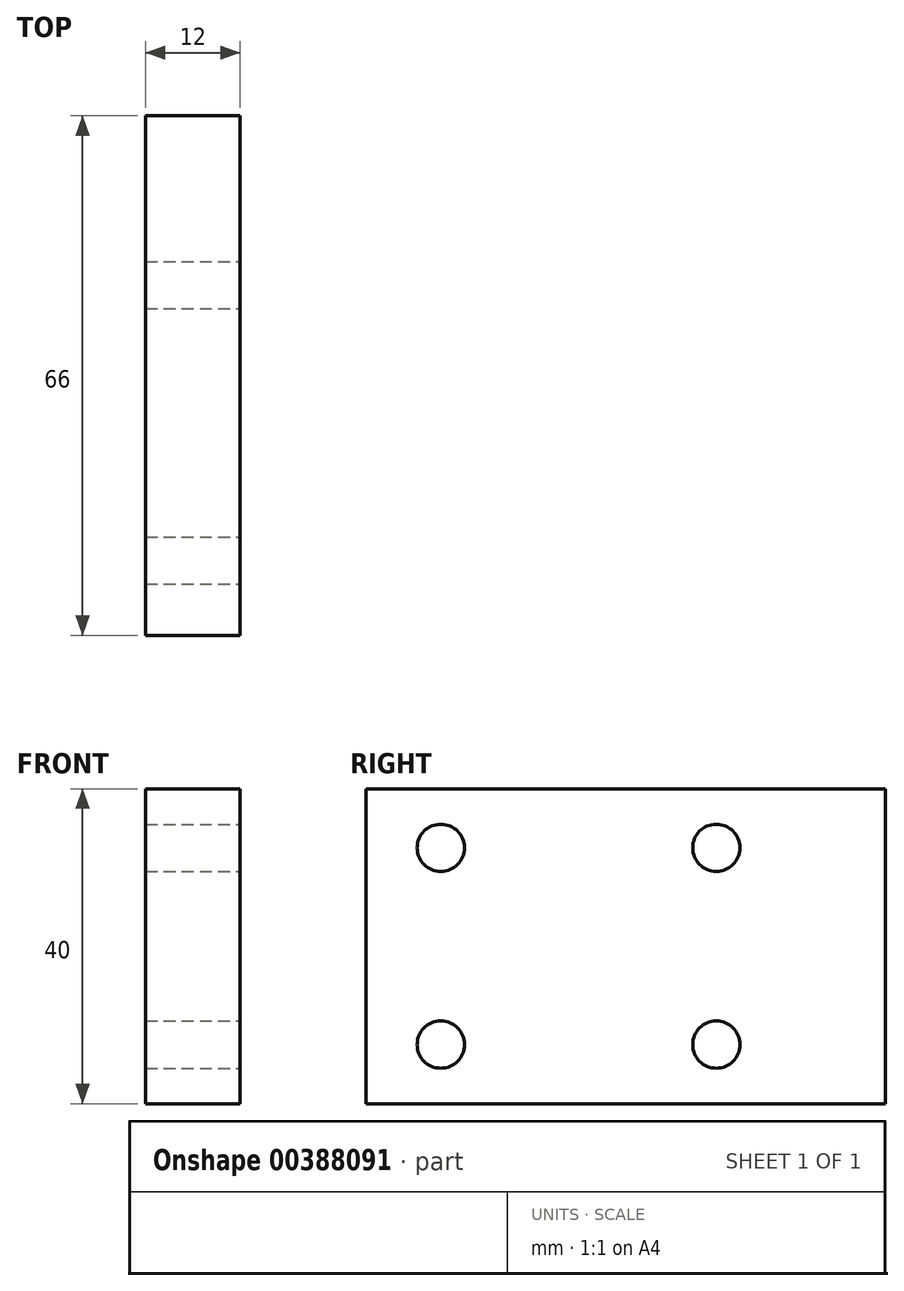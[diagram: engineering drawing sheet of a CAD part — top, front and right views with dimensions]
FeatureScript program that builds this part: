
annotation { "Feature Type Name" : "Feature", "Feature Type Description" : "" }
export const myFeature = defineFeature(function(context is Context, id is Id, definition is map)
    precondition{}
    {
        {
            var Q0;
            Q0=qCreatedBy(makeId("Right.planeOp"),FACE);
            var sketch = newSketch(context, id + "F0", { "sketchPlane" : qUnion([Q0])});
            skLineSegment(sketch, "E0.bottom", {"start": v(0, 0) * mm, "end": v(66, 0) * mm});
            skLineSegment(sketch, "E0.top", {"start": v(0, 40) * mm, "end": v(66, 40) * mm});
            skLineSegment(sketch, "E0.left", {"start": v(0, 0) * mm, "end": v(0, 40) * mm});
            skLineSegment(sketch, "E0.right", {"start": v(66, 0) * mm, "end": v(66, 40) * mm});
            skSolve(sketch);
        }
        {
            var Q0;
            Q0=makeQuery(id+"F0.imprint","IMPRINT",FACE,{"disambiguationData":[TD([[makeQuery(id+"F0.imprint","IMPRINT",EDGE,{"derivedFrom":sQuery(id+"F0.wireOp",EDGE,"E0.bottom")}),1.0]])]});
            extrude(context, id + "F1", {"entities" : qUnion([Q0]), "depth" : 12 * mm});
        }
        {
            var Q0;
            Q0=makeQuery(id+"F1.opExtrude","CAP_FACE",FACE,{"disambiguationData":[OSD([sQuery(id+"F0.wireOp",EDGE,"E0.bottom"),sQuery(id+"F0.wireOp",EDGE,"E0.top"),sQuery(id+"F0.wireOp",EDGE,"E0.left"),sQuery(id+"F0.wireOp",EDGE,"E0.right")])],"isStart":false});
            var sketch = newSketch(context, id + "F2", { "sketchPlane" : qUnion([Q0])});
            skLineSegment(sketch, "E1", {"start": v(0, 0) * mm, "end": v(9.5, 0) * mm, "construction": true});
            skLineSegment(sketch, "E2", {"start": v(9.5, 0) * mm, "end": v(9.5, 7.5) * mm, "construction": true});
            skLineSegment(sketch, "E3", {"start": v(9.5, 7.5) * mm, "end": v(9.5, 32.5) * mm, "construction": true});
            skLineSegment(sketch, "E4", {"start": v(9.5, 7.5) * mm, "end": v(44.5, 7.5) * mm, "construction": true});
            skLineSegment(sketch, "E5", {"start": v(44.5, 7.5) * mm, "end": v(44.5, 32.5) * mm, "construction": true});
            skSolve(sketch);
        }
        {
            var Q0;
            Q0=sQuery(id+"F2.wireOp",VERTEX,"E3.end");
            var Q1;
            Q1=sQuery(id+"F2.wireOp",VERTEX,"E4.start");
            var Q2;
            Q2=sQuery(id+"F2.wireOp",VERTEX,"E5.start");
            var Q3;
            Q3=sQuery(id+"F2.wireOp",VERTEX,"E5.end");
            var Q4;
            Q4=makeQuery(id+"F1.opExtrude","SWEPT_BODY",BODY,{"disambiguationData":[OSD([sQuery(id+"F0.wireOp",EDGE,"E0.bottom"),sQuery(id+"F0.wireOp",EDGE,"E0.top"),sQuery(id+"F0.wireOp",EDGE,"E0.left"),sQuery(id+"F0.wireOp",EDGE,"E0.right")])]});
            hole(context, id + "F3", {"style" : HoleStyle.SIMPLE, "endStyle" : HoleEndStyle.BLIND, "holeDiameter" : 6 * mm, "holeDepth" : 12 * mm, "isTappedThrough" : true, "tappedDepth" : 12 * mm, "tapClearance" : 3, "locations" : qUnion([Q0, Q1, Q2, Q3]), "scope" : qUnion([Q4])});
        }
    });
